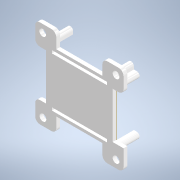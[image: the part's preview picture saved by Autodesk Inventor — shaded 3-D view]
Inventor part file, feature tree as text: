
AUTODESK INVENTOR PART (.ipt)
format: ipt  version: 2020 (Build 240168000, 168)  size: 256,512 bytes
history: native  units: in
note: dims shown in document units (in); Inventor stores cm internally (conversion verified against a paired STEP export)
features: reference x31, other x8, extrude x2, sketch x2, plane x1
ambient origin geometry x8: Origin, YZ Plane, XZ Plane, XY Plane, X Axis, Y Axis, Z Axis, Center Point
bodies: Solid1 (feature_tree)
feature tree (44):
  plane  "Work Plane1"
  extrude  "Extrusion2"  Depth=0.4545in TaperAngle=0.0deg
  extrude  "Extrusion3"  [1 undecoded]
  sketch  "Sketch2"  dims[d40=0.1in d41=0.0in d42=0.4545in d43=0.0in]
  sketch  "Sketch4"
  reference  "Reference10"
  reference  "Reference11"
  reference  "Reference12"
  reference  "Reference13"
  reference  "Reference14"
  reference  "Reference15"
  reference  "Reference16"
  reference  "Reference17"
  reference  "Reference18"
  reference  "Reference19"
  reference  "Reference20"
  reference  "Reference21"
  reference  "Reference22"
  reference  "Reference23"
  reference  "Reference24"
  reference  "Reference25"
  reference  "Reference26"
  reference  "Reference27"
  reference  "Reference28"
  reference  "Reference29"
  reference  "Reference30"
  reference  "Reference31"
  reference  "Reference32"
  reference  "Reference33"
  reference  "Reference34"
  reference  "Reference35"
  reference  "Reference36"
  reference  "Reference37"
  reference  "Reference38"
  reference  "Reference39"
  reference  "Reference40"
  other  "<userpath>\Documents\Inventor\Drone\Assembly.iam"
  other  "Assembly.iam"
  other  "standoff:1"
  other  "standoff:4"
  other  "standoff:2"
  other  "standoff:3"
  other  "holder:1"
  other  "Pixfalcon-Flight-Controller v1:1"
note: 1 required parameter value undecoded (feature->parameter linkage not recoverable at this tier; creation-order binding heuristic only, values carry confidence <= 0.55)
